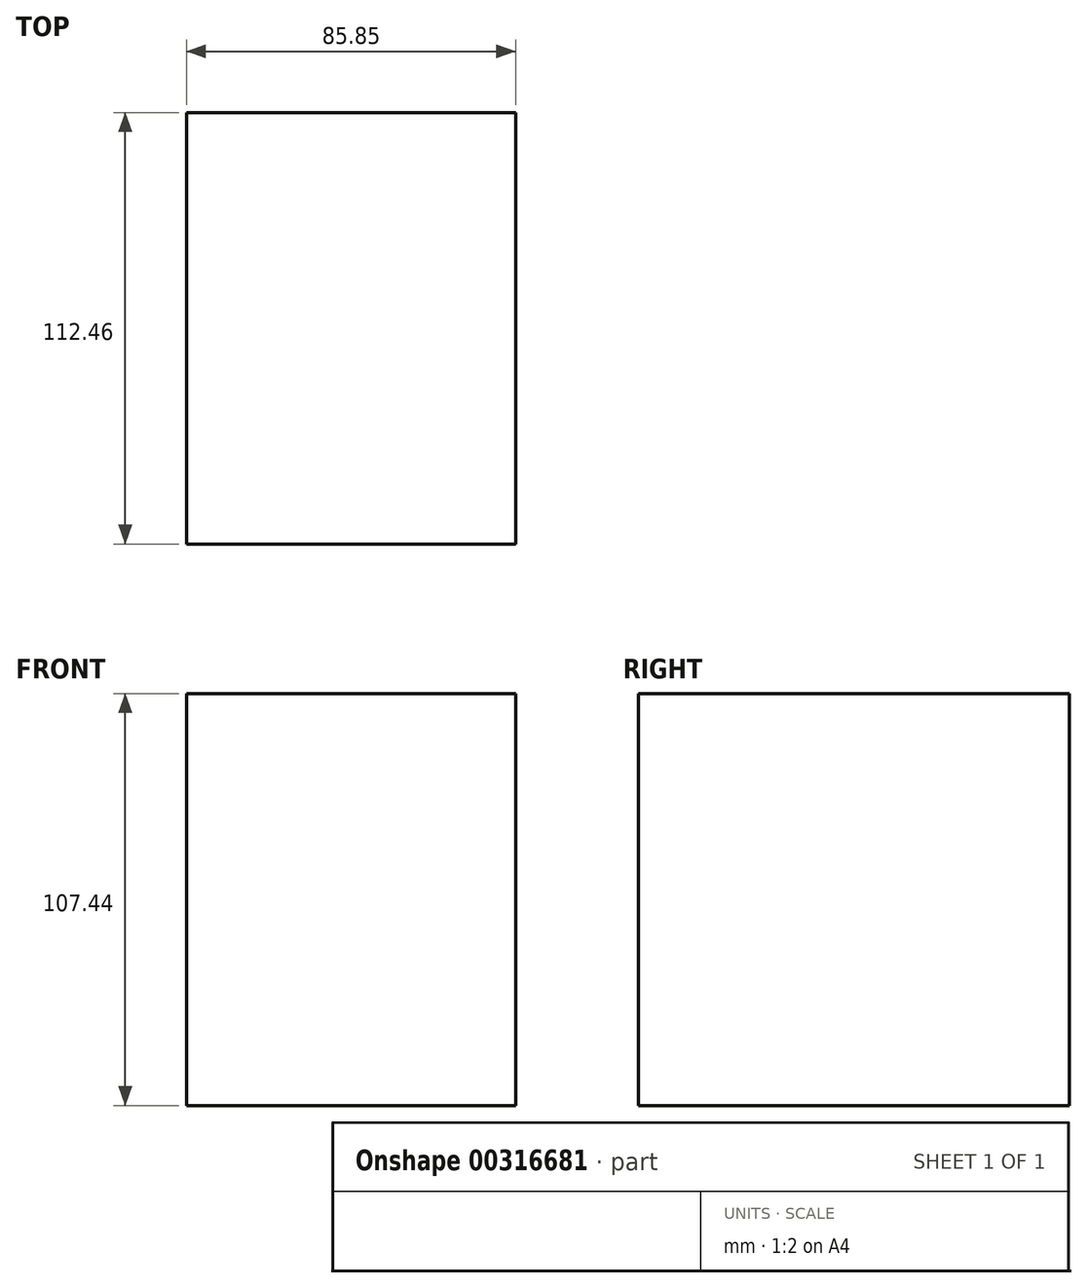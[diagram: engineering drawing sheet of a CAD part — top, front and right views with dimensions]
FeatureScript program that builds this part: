
annotation { "Feature Type Name" : "Feature", "Feature Type Description" : "" }
export const myFeature = defineFeature(function(context is Context, id is Id, definition is map)
    precondition{}
    {
        {
            var Q0;
            Q0=qCreatedBy(makeId("Top.planeOp"),FACE);
            var sketch = newSketch(context, id + "F0", { "sketchPlane" : qUnion([Q0])});
            skLineSegment(sketch, "E0.bottom", {"start": v(-40.06, 57.62) * mm, "end": v(45.79, 57.62) * mm});
            skLineSegment(sketch, "E0.top", {"start": v(-40.06, -54.84) * mm, "end": v(45.79, -54.84) * mm});
            skLineSegment(sketch, "E0.left", {"start": v(-40.06, 57.62) * mm, "end": v(-40.06, -54.84) * mm});
            skLineSegment(sketch, "E0.right", {"start": v(45.79, 57.62) * mm, "end": v(45.79, -54.84) * mm});
            skSolve(sketch);
        }
        {
            var Q0;
            Q0 = qSketchRegion(id + "F0", true);
            extrude(context, id + "F1", {"entities" : qUnion([Q0]), "oppositeDirection" : true, "depth" : 56.13 * mm, "hasSecondDirection" : true, "secondDirectionOppositeDirection" : false, "secondDirectionDepth" : 51.3 * mm});
        }
    });
